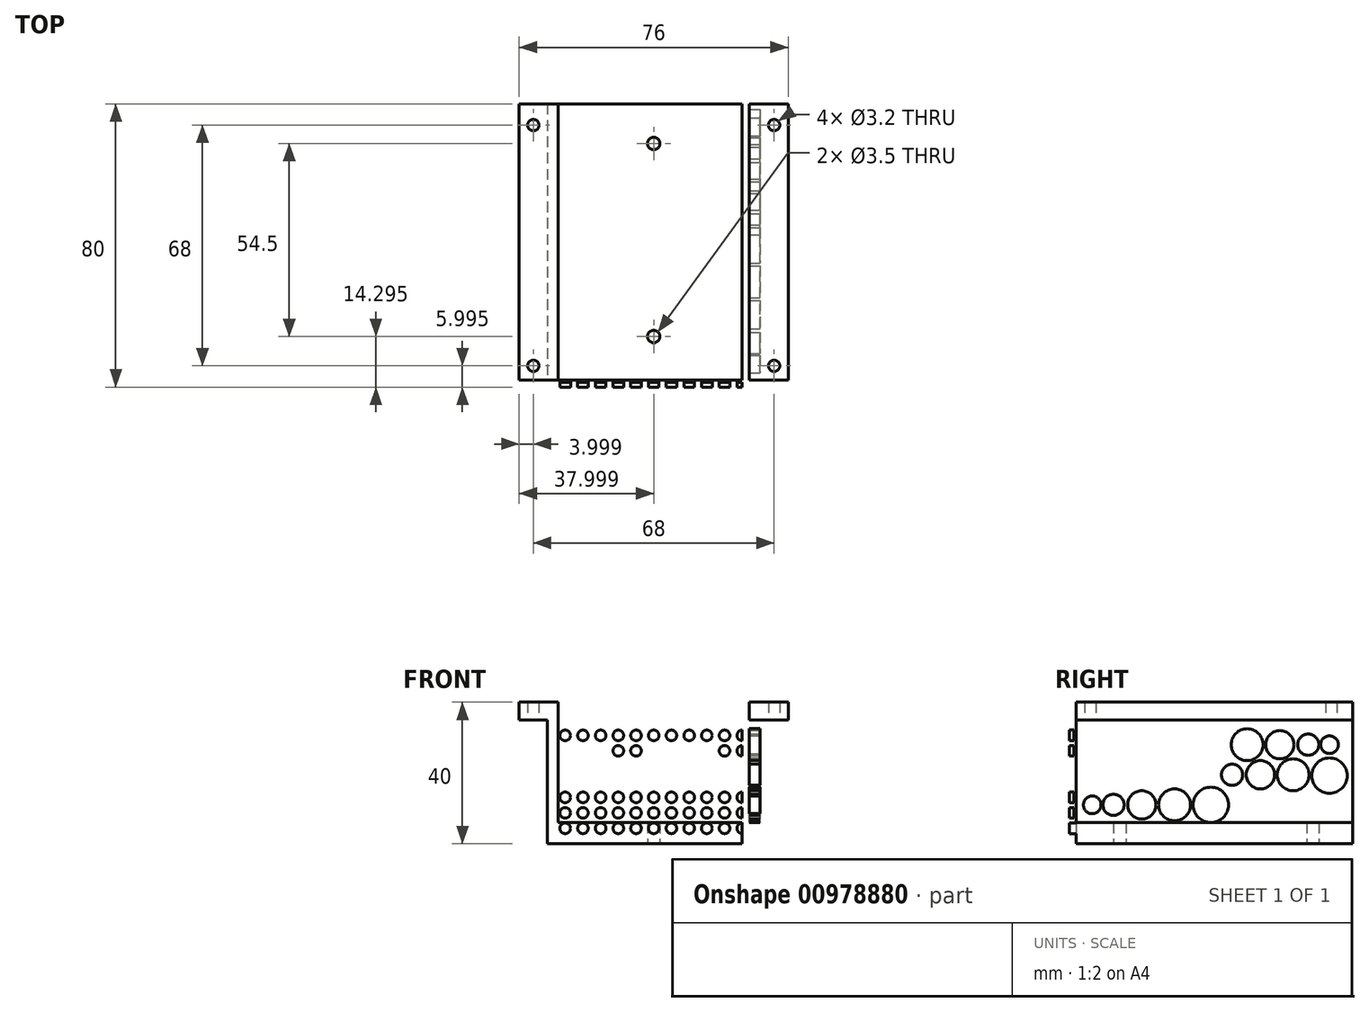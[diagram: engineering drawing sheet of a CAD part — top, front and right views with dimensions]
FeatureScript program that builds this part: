
annotation { "Feature Type Name" : "Feature", "Feature Type Description" : "" }
export const myFeature = defineFeature(function(context is Context, id is Id, definition is map)
    precondition{}
    {
        {
            var Q0;
            Q0=qCreatedBy(makeId("Top.planeOp"),FACE);
            var sketch = newSketch(context, id + "F0", { "sketchPlane" : qUnion([Q0])});
            skLineSegment(sketch, "E0.bottom", {"start": v(-26.48, 28.63) * mm, "end": v(33.52, 28.63) * mm});
            skLineSegment(sketch, "E0.top", {"start": v(-26.48, -51.37) * mm, "end": v(33.52, -51.37) * mm});
            skLineSegment(sketch, "E0.left", {"start": v(-26.48, 28.63) * mm, "end": v(-26.48, -51.37) * mm});
            skLineSegment(sketch, "E0.right", {"start": v(33.52, 28.63) * mm, "end": v(33.52, -51.37) * mm});
            skLineSegment(sketch, "E1", {"start": v(-23.48, 28.63) * mm, "end": v(-23.48, -51.37) * mm});
            skLineSegment(sketch, "E2", {"start": v(3.52, 28.63) * mm, "end": v(3.52, -51.37) * mm, "construction": true});
            skLineSegment(sketch, "E3", {"start": v(-26.48, -11.37) * mm, "end": v(33.52, -11.37) * mm, "construction": true});
            skLineSegment(sketch, "E4.MirrorCS", {"start": v(30.52, 28.63) * mm, "end": v(30.52, -51.37) * mm});
            skLineSegment(sketch, "E5", {"start": v(-23.48, -50.07) * mm, "end": v(30.52, -50.07) * mm});
            skCircle(sketch, "E6", {"center": v(3.52, -37.07) * mm, "radius": 1.75 * mm});
            skCircle(sketch, "E7", {"center": v(3.52, 17.43) * mm, "radius": 1.75 * mm});
            skLineSegment(sketch, "E8", {"start": v(-26.48, 28.63) * mm, "end": v(-34.48, 28.63) * mm});
            skLineSegment(sketch, "E9", {"start": v(-34.48, 28.63) * mm, "end": v(-34.48, -51.37) * mm});
            skLineSegment(sketch, "E10", {"start": v(-34.48, -51.37) * mm, "end": v(-26.48, -51.37) * mm});
            skLineSegment(sketch, "E11.MirrorCS", {"start": v(41.52, 28.63) * mm, "end": v(41.52, -51.37) * mm});
            skLineSegment(sketch, "E12.MirrorCS", {"start": v(33.52, 28.63) * mm, "end": v(41.52, 28.63) * mm});
            skLineSegment(sketch, "E13.MirrorCS", {"start": v(41.52, -51.37) * mm, "end": v(33.52, -51.37) * mm});
            skCircle(sketch, "E14", {"center": v(-30.48, 22.63) * mm, "radius": 1.6 * mm});
            skLineSegment(sketch, "E15", {"start": v(-34.48, -11.37) * mm, "end": v(41.52, -11.37) * mm, "construction": true});
            skCircle(sketch, "E16.MirrorC", {"center": v(-30.48, -45.37) * mm, "radius": 1.6 * mm});
            skCircle(sketch, "E17.MirrorC", {"center": v(37.52, 22.63) * mm, "radius": 1.6 * mm});
            skCircle(sketch, "E18.MirrorC", {"center": v(37.52, -45.37) * mm, "radius": 1.6 * mm});
            skSolve(sketch);
        }
        {
            var Q0;
            {var subQ0=sQuery(id+"F0.wireOp",EDGE,"E0.left");Q0=makeQuery(id+"F0.imprint","IMPRINT",FACE,{"disambiguationData":[TD([[makeQuery(id+"F0.imprint","IMPRINT",EDGE,{"derivedFrom":subQ0}),1.0]])]});}
            var Q1;
            {var subQ4=sQuery(id+"F0.wireOp",EDGE,"E0.right");Q1=makeQuery(id+"F0.imprint","IMPRINT",FACE,{"disambiguationData":[TD([[makeQuery(id+"F0.imprint","IMPRINT",EDGE,{"derivedFrom":subQ4}),-1.0]])]});}
            var Q2;
            {var subQ5=sQuery(id+"F0.wireOp",EDGE,"E5");Q2=makeQuery(id+"F0.imprint","IMPRINT",FACE,{"disambiguationData":[TD([[makeQuery(id+"F0.imprint","IMPRINT",EDGE,{"derivedFrom":subQ5}),-1.0]])]});}
            extrude(context, id + "F1", {"entities" : qUnion([Q0, Q1, Q2]), "depth" : 40 * mm, "offsetDistance" : 25 * mm});
        }
        {
            var Q0;
            {var subQ5=sQuery(id+"F0.wireOp",EDGE,"E5");Q0=makeQuery(id+"F0.imprint","IMPRINT",FACE,{"disambiguationData":[TD([[makeQuery(id+"F0.imprint","IMPRINT",EDGE,{"derivedFrom":subQ5}),1.0]])]});}
            extrude(context, id + "F2", {"entities" : qUnion([Q0]), "operationType" : NewBodyOperationType.ADD, "depth" : 6 * mm, "offsetDistance" : 25 * mm});
        }
        {
            var Q0;
            Q0=makeQuery(id+"F0.imprint","IMPRINT",FACE,{"disambiguationData":[TD([[makeQuery(id+"F0.imprint","IMPRINT",EDGE,{"derivedFrom":sQuery(id+"F0.wireOp",EDGE,"E0.left")}),-1.0]])]});
            var Q1;
            Q1=makeQuery(id+"F0.imprint","IMPRINT",FACE,{"disambiguationData":[TD([[makeQuery(id+"F0.imprint","IMPRINT",EDGE,{"derivedFrom":sQuery(id+"F0.wireOp",EDGE,"E0.right")}),1.0]])]});
            extrude(context, id + "F3", {"entities" : qUnion([Q0, Q1]), "operationType" : NewBodyOperationType.ADD, "depth" : 40 * mm, "offsetDistance" : 25 * mm, "hasSecondDirection" : true, "secondDirectionOppositeDirection" : false, "secondDirectionDepth" : 35 * mm});
        }
        {
            var Q0;
            Q0=makeQuery(id+"F1.opExtrude","SWEPT_FACE",FACE,{"disambiguationData":[OSD([sQuery(id+"F0.wireOp",EDGE,"E0.right")])]});
            var sketch = newSketch(context, id + "F4", { "sketchPlane" : qUnion([Q0])});
            skLineSegment(sketch, "E19", {"start": v(-11.37, 35) * mm, "end": v(-11.37, 0) * mm, "construction": true});
            skCircle(sketch, "E20", {"center": v(-11.37, 28) * mm, "radius": 5 * mm});
            skCircle(sketch, "E21", {"center": v(-11.37, 19.5) * mm, "radius": 2.5 * mm});
            skLineSegment(sketch, "E22", {"start": v(-44.87, 39) * mm, "end": v(-44.87, 0) * mm, "construction": true});
            skLineSegment(sketch, "E23", {"start": v(-38.26, 35) * mm, "end": v(-38.26, 0) * mm, "construction": true});
            skLineSegment(sketch, "E24", {"start": v(-25.37, 39) * mm, "end": v(-25.37, 0) * mm, "construction": true});
            skLineSegment(sketch, "E25", {"start": v(-21.54, 35) * mm, "end": v(-21.54, 0) * mm, "construction": true});
            skCircle(sketch, "E26", {"center": v(-17.37, 19.5) * mm, "radius": 3 * mm});
            skCircle(sketch, "E27", {"center": v(-25.37, 19.5) * mm, "radius": 4 * mm});
            skCircle(sketch, "E28", {"center": v(-44.87, 19.5) * mm, "radius": 5 * mm});
            skCircle(sketch, "E29", {"center": v(-34.62, 19.5) * mm, "radius": 4.5 * mm});
            skCircle(sketch, "E30.MirrorC", {"center": v(-5.37, 19.5) * mm, "radius": 3 * mm});
            skCircle(sketch, "E31.MirrorC", {"center": v(2.63, 19.5) * mm, "radius": 4 * mm});
            skCircle(sketch, "E32.MirrorC", {"center": v(11.88, 19.5) * mm, "radius": 4.5 * mm});
            skCircle(sketch, "E33.MirrorC", {"center": v(22.13, 19.25) * mm, "radius": 5 * mm});
            skCircle(sketch, "E34", {"center": v(-21.62, 28) * mm, "radius": 4.5 * mm});
            skCircle(sketch, "E35", {"center": v(-30.87, 28) * mm, "radius": 4 * mm});
            skCircle(sketch, "E36", {"center": v(-38.87, 28) * mm, "radius": 3 * mm});
            skCircle(sketch, "E37", {"center": v(-44.87, 28) * mm, "radius": 2.5 * mm});
            skCircle(sketch, "E38.MirrorC", {"center": v(-1.12, 28) * mm, "radius": 4.5 * mm});
            skCircle(sketch, "E39.MirrorC", {"center": v(8.13, 28) * mm, "radius": 4 * mm});
            skCircle(sketch, "E40.MirrorC", {"center": v(16.13, 28) * mm, "radius": 3 * mm});
            skCircle(sketch, "E41.MirrorC", {"center": v(22.13, 28) * mm, "radius": 2.5 * mm});
            skLineSegment(sketch, "E42", {"start": v(-51.37, 19.5) * mm, "end": v(28.63, 19.5) * mm, "construction": true});
            skCircle(sketch, "E43.MirrorC", {"center": v(-11.37, 11) * mm, "radius": 5 * mm});
            skCircle(sketch, "E44.MirrorC", {"center": v(-21.62, 11) * mm, "radius": 4.5 * mm});
            skCircle(sketch, "E45.MirrorC", {"center": v(-30.87, 11) * mm, "radius": 4 * mm});
            skCircle(sketch, "E46.MirrorC", {"center": v(-38.87, 11) * mm, "radius": 3 * mm});
            skCircle(sketch, "E47.MirrorC", {"center": v(-44.87, 11) * mm, "radius": 2.5 * mm});
            skCircle(sketch, "E48.MirrorC", {"center": v(-1.12, 11) * mm, "radius": 4.5 * mm});
            skCircle(sketch, "E49.MirrorC", {"center": v(8.13, 11) * mm, "radius": 4 * mm});
            skCircle(sketch, "E50.MirrorC", {"center": v(16.13, 11) * mm, "radius": 3 * mm});
            skCircle(sketch, "E51.MirrorC", {"center": v(22.13, 11) * mm, "radius": 2.5 * mm});
            skLineSegment(sketch, "E52", {"start": v(-11.37, 28) * mm, "end": v(-51.37, 28) * mm, "construction": true});
            skLineSegment(sketch, "E53", {"start": v(-51.37, 28) * mm, "end": v(28.63, 28) * mm, "construction": true});
            skSolve(sketch);
        }
        {
            var Q0;
            Q0=makeQuery(id+"F4.imprint","IMPRINT",FACE,{"disambiguationData":[TD([[makeQuery(id+"F4.imprint","IMPRINT",EDGE,{"derivedFrom":sQuery(id+"F4.wireOp",EDGE,"E37")}),1.0]])]});
            var Q1;
            Q1=makeQuery(id+"F4.imprint","IMPRINT",FACE,{"disambiguationData":[TD([[makeQuery(id+"F4.imprint","IMPRINT",EDGE,{"derivedFrom":sQuery(id+"F4.wireOp",EDGE,"E36")}),1.0]])]});
            var Q2;
            Q2=makeQuery(id+"F4.imprint","IMPRINT",FACE,{"disambiguationData":[TD([[makeQuery(id+"F4.imprint","IMPRINT",EDGE,{"derivedFrom":sQuery(id+"F4.wireOp",EDGE,"E35")}),1.0]])]});
            var Q3;
            Q3=makeQuery(id+"F4.imprint","IMPRINT",FACE,{"disambiguationData":[TD([[makeQuery(id+"F4.imprint","IMPRINT",EDGE,{"derivedFrom":sQuery(id+"F4.wireOp",EDGE,"E34")}),1.0]])]});
            var Q4;
            Q4=makeQuery(id+"F4.imprint","IMPRINT",FACE,{"disambiguationData":[TD([[makeQuery(id+"F4.imprint","IMPRINT",EDGE,{"derivedFrom":sQuery(id+"F4.wireOp",EDGE,"E20")}),1.0]])]});
            var Q5;
            Q5=makeQuery(id+"F4.imprint","IMPRINT",FACE,{"disambiguationData":[TD([[makeQuery(id+"F4.imprint","IMPRINT",EDGE,{"derivedFrom":sQuery(id+"F4.wireOp",EDGE,"E21")}),1.0]])]});
            var Q6;
            Q6=makeQuery(id+"F4.imprint","IMPRINT",FACE,{"disambiguationData":[TD([[makeQuery(id+"F4.imprint","IMPRINT",EDGE,{"derivedFrom":sQuery(id+"F4.wireOp",EDGE,"E26")}),1.0]])]});
            var Q7;
            Q7=makeQuery(id+"F4.imprint","IMPRINT",FACE,{"disambiguationData":[TD([[makeQuery(id+"F4.imprint","IMPRINT",EDGE,{"derivedFrom":sQuery(id+"F4.wireOp",EDGE,"E27")}),1.0]])]});
            var Q8;
            Q8=makeQuery(id+"F4.imprint","IMPRINT",FACE,{"disambiguationData":[TD([[makeQuery(id+"F4.imprint","IMPRINT",EDGE,{"derivedFrom":sQuery(id+"F4.wireOp",EDGE,"E29")}),1.0]])]});
            var Q9;
            Q9=makeQuery(id+"F4.imprint","IMPRINT",FACE,{"disambiguationData":[TD([[makeQuery(id+"F4.imprint","IMPRINT",EDGE,{"derivedFrom":sQuery(id+"F4.wireOp",EDGE,"E28")}),1.0]])]});
            var Q10;
            Q10=makeQuery(id+"F4.imprint","IMPRINT",FACE,{"disambiguationData":[TD([[makeQuery(id+"F4.imprint","IMPRINT",EDGE,{"derivedFrom":sQuery(id+"F4.wireOp",EDGE,"d2b82f4c-cb30-4b27-9ca2-75d97dd168ee0.MirrorC")}),-1.0]])]});
            var Q11;
            Q11=makeQuery(id+"F4.imprint","IMPRINT",FACE,{"disambiguationData":[TD([[makeQuery(id+"F4.imprint","IMPRINT",EDGE,{"derivedFrom":sQuery(id+"F4.wireOp",EDGE,"6bd1dfd8-2cc8-4437-9d2b-2d223e5973cc0.MirrorC")}),-1.0]])]});
            var Q12;
            Q12=makeQuery(id+"F4.imprint","IMPRINT",FACE,{"disambiguationData":[TD([[makeQuery(id+"F4.imprint","IMPRINT",EDGE,{"derivedFrom":sQuery(id+"F4.wireOp",EDGE,"112abbcc-eb7b-4c05-a6dc-7863f32487d60.MirrorC")}),-1.0]])]});
            var Q13;
            Q13=makeQuery(id+"F4.imprint","IMPRINT",FACE,{"disambiguationData":[TD([[makeQuery(id+"F4.imprint","IMPRINT",EDGE,{"derivedFrom":sQuery(id+"F4.wireOp",EDGE,"63fc9d48-1385-4d69-bd1f-f335cad14c7e0.MirrorC")}),-1.0]])]});
            var Q14;
            Q14=makeQuery(id+"F4.imprint","IMPRINT",FACE,{"disambiguationData":[TD([[makeQuery(id+"F4.imprint","IMPRINT",EDGE,{"derivedFrom":sQuery(id+"F4.wireOp",EDGE,"CqitQkb0-iUWd-npEw-QbOA-i5By9fwf5P85")}),1.0]])]});
            var Q15;
            Q15=makeQuery(id+"F4.imprint","IMPRINT",FACE,{"disambiguationData":[TD([[makeQuery(id+"F4.imprint","IMPRINT",EDGE,{"derivedFrom":sQuery(id+"F4.wireOp",EDGE,"b05cfdfd-f439-45fa-b4f9-9b1710cce5d10.MirrorC")}),1.0]])]});
            var Q16;
            Q16=makeQuery(id+"F4.imprint","IMPRINT",FACE,{"disambiguationData":[TD([[makeQuery(id+"F4.imprint","IMPRINT",EDGE,{"derivedFrom":sQuery(id+"F4.wireOp",EDGE,"E30.MirrorC")}),-1.0]])]});
            var Q17;
            Q17=makeQuery(id+"F4.imprint","IMPRINT",FACE,{"disambiguationData":[TD([[makeQuery(id+"F4.imprint","IMPRINT",EDGE,{"derivedFrom":sQuery(id+"F4.wireOp",EDGE,"E38.MirrorC")}),-1.0]])]});
            var Q18;
            Q18=makeQuery(id+"F4.imprint","IMPRINT",FACE,{"disambiguationData":[TD([[makeQuery(id+"F4.imprint","IMPRINT",EDGE,{"derivedFrom":sQuery(id+"F4.wireOp",EDGE,"E31.MirrorC")}),-1.0]])]});
            var Q19;
            Q19=makeQuery(id+"F4.imprint","IMPRINT",FACE,{"disambiguationData":[TD([[makeQuery(id+"F4.imprint","IMPRINT",EDGE,{"derivedFrom":sQuery(id+"F4.wireOp",EDGE,"2864415c-c3ac-41cb-945e-1ae6a54a86a40.MirrorC")}),1.0]])]});
            var Q20;
            Q20=makeQuery(id+"F4.imprint","IMPRINT",FACE,{"disambiguationData":[TD([[makeQuery(id+"F4.imprint","IMPRINT",EDGE,{"derivedFrom":sQuery(id+"F4.wireOp",EDGE,"E32.MirrorC")}),-1.0]])]});
            var Q21;
            Q21=makeQuery(id+"F4.imprint","IMPRINT",FACE,{"disambiguationData":[TD([[makeQuery(id+"F4.imprint","IMPRINT",EDGE,{"derivedFrom":sQuery(id+"F4.wireOp",EDGE,"E39.MirrorC")}),-1.0]])]});
            var Q22;
            Q22=makeQuery(id+"F4.imprint","IMPRINT",FACE,{"disambiguationData":[TD([[makeQuery(id+"F4.imprint","IMPRINT",EDGE,{"derivedFrom":sQuery(id+"F4.wireOp",EDGE,"E40.MirrorC")}),-1.0]])]});
            var Q23;
            Q23=makeQuery(id+"F4.imprint","IMPRINT",FACE,{"disambiguationData":[TD([[makeQuery(id+"F4.imprint","IMPRINT",EDGE,{"derivedFrom":sQuery(id+"F4.wireOp",EDGE,"E41.MirrorC")}),-1.0]])]});
            var Q24;
            Q24=makeQuery(id+"F4.imprint","IMPRINT",FACE,{"disambiguationData":[TD([[makeQuery(id+"F4.imprint","IMPRINT",EDGE,{"derivedFrom":sQuery(id+"F4.wireOp",EDGE,"E33.MirrorC")}),-1.0]])]});
            var Q25;
            Q25=makeQuery(id+"F4.imprint","IMPRINT",FACE,{"disambiguationData":[TD([[makeQuery(id+"F4.imprint","IMPRINT",EDGE,{"derivedFrom":sQuery(id+"F4.wireOp",EDGE,"b64800c5-5fc1-485e-8181-1b029b5031790.MirrorC")}),1.0]])]});
            var Q26;
            Q26=makeQuery(id+"F4.imprint","IMPRINT",FACE,{"disambiguationData":[TD([[makeQuery(id+"F4.imprint","IMPRINT",EDGE,{"derivedFrom":sQuery(id+"F4.wireOp",EDGE,"3597d698-ec06-4dc3-ab4d-8b58906ce14e0.MirrorC")}),1.0]])]});
            var Q27;
            Q27=makeQuery(id+"F4.imprint","IMPRINT",FACE,{"disambiguationData":[TD([[makeQuery(id+"F4.imprint","IMPRINT",EDGE,{"derivedFrom":sQuery(id+"F4.wireOp",EDGE,"E47.MirrorC")}),-1.0]])]});
            var Q28;
            Q28=makeQuery(id+"F4.imprint","IMPRINT",FACE,{"disambiguationData":[TD([[makeQuery(id+"F4.imprint","IMPRINT",EDGE,{"derivedFrom":sQuery(id+"F4.wireOp",EDGE,"E46.MirrorC")}),-1.0]])]});
            var Q29;
            Q29=makeQuery(id+"F4.imprint","IMPRINT",FACE,{"disambiguationData":[TD([[makeQuery(id+"F4.imprint","IMPRINT",EDGE,{"derivedFrom":sQuery(id+"F4.wireOp",EDGE,"E45.MirrorC")}),-1.0]])]});
            var Q30;
            Q30=makeQuery(id+"F4.imprint","IMPRINT",FACE,{"disambiguationData":[TD([[makeQuery(id+"F4.imprint","IMPRINT",EDGE,{"derivedFrom":sQuery(id+"F4.wireOp",EDGE,"E44.MirrorC")}),-1.0]])]});
            var Q31;
            Q31=makeQuery(id+"F4.imprint","IMPRINT",FACE,{"disambiguationData":[TD([[makeQuery(id+"F4.imprint","IMPRINT",EDGE,{"derivedFrom":sQuery(id+"F4.wireOp",EDGE,"E43.MirrorC")}),-1.0]])]});
            var Q32;
            Q32=makeQuery(id+"F4.imprint","IMPRINT",FACE,{"disambiguationData":[TD([[makeQuery(id+"F4.imprint","IMPRINT",EDGE,{"derivedFrom":sQuery(id+"F4.wireOp",EDGE,"E48.MirrorC")}),1.0]])]});
            var Q33;
            Q33=makeQuery(id+"F4.imprint","IMPRINT",FACE,{"disambiguationData":[TD([[makeQuery(id+"F4.imprint","IMPRINT",EDGE,{"derivedFrom":sQuery(id+"F4.wireOp",EDGE,"E49.MirrorC")}),1.0]])]});
            var Q34;
            Q34=makeQuery(id+"F4.imprint","IMPRINT",FACE,{"disambiguationData":[TD([[makeQuery(id+"F4.imprint","IMPRINT",EDGE,{"derivedFrom":sQuery(id+"F4.wireOp",EDGE,"E50.MirrorC")}),1.0]])]});
            var Q35;
            Q35=makeQuery(id+"F4.imprint","IMPRINT",FACE,{"disambiguationData":[TD([[makeQuery(id+"F4.imprint","IMPRINT",EDGE,{"derivedFrom":sQuery(id+"F4.wireOp",EDGE,"E51.MirrorC")}),1.0]])]});
            extrude(context, id + "F5", {"entities" : qUnion([Q0, Q1, Q2, Q3, Q4, Q5, Q6, Q7, Q8, Q9, Q10, Q11, Q12, Q13, Q14, Q15, Q16, Q17, Q18, Q19, Q20, Q21, Q22, Q23, Q24, Q25, Q26, Q27, Q28, Q29, Q30, Q31, Q32, Q33, Q34, Q35]), "operationType" : NewBodyOperationType.REMOVE, "oppositeDirection" : true, "depth" : 5 * mm, "offsetDistance" : 25 * mm});
        }
        {
            var Q0;
            Q0=makeQuery(id+"F3.boolean.opBoolean","MERGE",FACE,{"derivedFrom":[makeQuery(id+"F1.opExtrude","SWEPT_FACE",FACE,{"disambiguationData":[OSD([sQuery(id+"F0.wireOp",EDGE,"E0.top")])]}),makeQuery(id+"F3.opExtrude","SWEPT_FACE",FACE,{"disambiguationData":[OSD([sQuery(id+"F0.wireOp",EDGE,"E10")])]}),makeQuery(id+"F3.opExtrude","SWEPT_FACE",FACE,{"disambiguationData":[OSD([sQuery(id+"F0.wireOp",EDGE,"E13.MirrorCS")])]})]});
            var sketch = newSketch(context, id + "F6", { "sketchPlane" : qUnion([Q0])});
            skLineSegment(sketch, "E54", {"start": v(3.52, 40) * mm, "end": v(3.52, 0) * mm, "construction": true});
            skLineSegment(sketch, "E55", {"start": v(-26.48, 17.5) * mm, "end": v(33.52, 17.5) * mm, "construction": true});
            skLineSegment(sketch, "E56", {"start": v(-26.48, 35) * mm, "end": v(33.52, 35) * mm, "construction": true});
            skLineSegment(sketch, "E57", {"start": v(-26.48, 30.62) * mm, "end": v(33.52, 30.63) * mm, "construction": true});
            skLineSegment(sketch, "E58", {"start": v(33.52, 26.25) * mm, "end": v(-26.48, 26.25) * mm, "construction": true});
            skLineSegment(sketch, "E59", {"start": v(-26.48, 21.88) * mm, "end": v(33.52, 21.88) * mm, "construction": true});
            skLineSegment(sketch, "E60", {"start": v(-1.48, 35) * mm, "end": v(-1.48, 0) * mm, "construction": true});
            skLineSegment(sketch, "E61", {"start": v(-6.48, 35) * mm, "end": v(-6.48, 0) * mm, "construction": true});
            skLineSegment(sketch, "E62", {"start": v(-11.48, 35) * mm, "end": v(-11.48, 0) * mm, "construction": true});
            skLineSegment(sketch, "E63", {"start": v(-16.48, 35) * mm, "end": v(-16.48, 0) * mm, "construction": true});
            skLineSegment(sketch, "E64", {"start": v(-21.48, 35) * mm, "end": v(-21.48, 0) * mm, "construction": true});
            skLineSegment(sketch, "E65.MirrorCS", {"start": v(8.52, 35) * mm, "end": v(8.52, 0) * mm, "construction": true});
            skLineSegment(sketch, "E66.MirrorCS", {"start": v(13.52, 35) * mm, "end": v(13.52, 0) * mm, "construction": true});
            skLineSegment(sketch, "E67.MirrorCS", {"start": v(18.52, 35) * mm, "end": v(18.52, 0) * mm, "construction": true});
            skLineSegment(sketch, "E68.MirrorCS", {"start": v(23.52, 35) * mm, "end": v(23.52, 0) * mm, "construction": true});
            skLineSegment(sketch, "E69.MirrorCS", {"start": v(28.52, 35) * mm, "end": v(28.52, 0) * mm, "construction": true});
            skLineSegment(sketch, "E70.MirrorCS", {"start": v(-26.48, 13.12) * mm, "end": v(33.52, 13.12) * mm, "construction": true});
            skLineSegment(sketch, "E71.MirrorCS", {"start": v(33.52, 8.75) * mm, "end": v(-26.48, 8.75) * mm, "construction": true});
            skLineSegment(sketch, "E72.MirrorCS", {"start": v(-26.48, 4.38) * mm, "end": v(33.52, 4.37) * mm, "construction": true});
            skCircle(sketch, "E73", {"center": v(-21.48, 35) * mm, "radius": 1.5 * mm});
            skCircle(sketch, "E74", {"center": v(-16.48, 35) * mm, "radius": 1.5 * mm});
            skCircle(sketch, "E75", {"center": v(-11.48, 35) * mm, "radius": 1.5 * mm});
            skCircle(sketch, "E76", {"center": v(-6.48, 35) * mm, "radius": 1.5 * mm});
            skCircle(sketch, "E77", {"center": v(-1.48, 35) * mm, "radius": 1.5 * mm});
            skCircle(sketch, "E78", {"center": v(3.52, 35) * mm, "radius": 1.5 * mm});
            skCircle(sketch, "E79", {"center": v(8.52, 35) * mm, "radius": 1.5 * mm});
            skCircle(sketch, "E80", {"center": v(13.52, 35) * mm, "radius": 1.5 * mm});
            skCircle(sketch, "E81", {"center": v(18.52, 35) * mm, "radius": 1.5 * mm});
            skCircle(sketch, "E82", {"center": v(23.52, 35) * mm, "radius": 1.5 * mm});
            skCircle(sketch, "E83", {"center": v(28.52, 35) * mm, "radius": 1.5 * mm});
            skCircle(sketch, "E84.MirrorC", {"center": v(-21.48, 26.25) * mm, "radius": 1.5 * mm});
            skCircle(sketch, "E85.MirrorC", {"center": v(-16.48, 26.25) * mm, "radius": 1.5 * mm});
            skCircle(sketch, "E86.MirrorC", {"center": v(-11.48, 26.25) * mm, "radius": 1.5 * mm});
            skCircle(sketch, "E87.MirrorC", {"center": v(-6.48, 26.25) * mm, "radius": 1.5 * mm});
            skCircle(sketch, "E88.MirrorC", {"center": v(-1.48, 26.25) * mm, "radius": 1.5 * mm});
            skCircle(sketch, "E89.MirrorC", {"center": v(3.52, 26.25) * mm, "radius": 1.5 * mm});
            skCircle(sketch, "E90.MirrorC", {"center": v(8.52, 26.25) * mm, "radius": 1.5 * mm});
            skCircle(sketch, "E91.MirrorC", {"center": v(13.52, 26.25) * mm, "radius": 1.5 * mm});
            skCircle(sketch, "E92.MirrorC", {"center": v(18.52, 26.25) * mm, "radius": 1.5 * mm});
            skCircle(sketch, "E93.MirrorC", {"center": v(23.52, 26.25) * mm, "radius": 1.5 * mm});
            skCircle(sketch, "E94.MirrorC", {"center": v(28.52, 26.25) * mm, "radius": 1.5 * mm});
            skCircle(sketch, "E95.MirrorC", {"center": v(-21.48, 17.5) * mm, "radius": 1.5 * mm});
            skCircle(sketch, "E96.MirrorC", {"center": v(-16.48, 17.5) * mm, "radius": 1.5 * mm});
            skCircle(sketch, "E97.MirrorC", {"center": v(-11.48, 17.5) * mm, "radius": 1.5 * mm});
            skCircle(sketch, "E98.MirrorC", {"center": v(-6.48, 17.5) * mm, "radius": 1.5 * mm});
            skCircle(sketch, "E99.MirrorC", {"center": v(-1.48, 17.5) * mm, "radius": 1.5 * mm});
            skCircle(sketch, "E100.MirrorC", {"center": v(3.52, 17.5) * mm, "radius": 1.5 * mm});
            skCircle(sketch, "E101.MirrorC", {"center": v(8.52, 17.5) * mm, "radius": 1.5 * mm});
            skCircle(sketch, "E102.MirrorC", {"center": v(13.52, 17.5) * mm, "radius": 1.5 * mm});
            skCircle(sketch, "E103.MirrorC", {"center": v(18.52, 17.5) * mm, "radius": 1.5 * mm});
            skCircle(sketch, "E104.MirrorC", {"center": v(23.52, 17.5) * mm, "radius": 1.5 * mm});
            skCircle(sketch, "E105.MirrorC", {"center": v(28.52, 17.5) * mm, "radius": 1.5 * mm});
            skCircle(sketch, "E106.MirrorC", {"center": v(28.52, 8.75) * mm, "radius": 1.5 * mm});
            skCircle(sketch, "E107.MirrorC", {"center": v(23.52, 8.75) * mm, "radius": 1.5 * mm});
            skCircle(sketch, "E108.MirrorC", {"center": v(18.52, 8.75) * mm, "radius": 1.5 * mm});
            skCircle(sketch, "E109.MirrorC", {"center": v(13.52, 8.75) * mm, "radius": 1.5 * mm});
            skCircle(sketch, "E110.MirrorC", {"center": v(8.52, 8.75) * mm, "radius": 1.5 * mm});
            skCircle(sketch, "E111.MirrorC", {"center": v(3.52, 8.75) * mm, "radius": 1.5 * mm});
            skCircle(sketch, "E112.MirrorC", {"center": v(-1.48, 8.75) * mm, "radius": 1.5 * mm});
            skCircle(sketch, "E113.MirrorC", {"center": v(-6.48, 8.75) * mm, "radius": 1.5 * mm});
            skCircle(sketch, "E114.MirrorC", {"center": v(-21.48, 8.75) * mm, "radius": 1.5 * mm});
            skCircle(sketch, "E115.MirrorC", {"center": v(-16.48, 8.75) * mm, "radius": 1.5 * mm});
            skCircle(sketch, "E116.MirrorC", {"center": v(-11.48, 8.75) * mm, "radius": 1.5 * mm});
            skLineSegment(sketch, "E117", {"start": v(-26.48, 32.81) * mm, "end": v(33.52, 32.81) * mm, "construction": true});
            skCircle(sketch, "E118.MirrorC", {"center": v(8.52, 30.62) * mm, "radius": 1.5 * mm});
            skCircle(sketch, "E119.MirrorC", {"center": v(-21.48, 30.62) * mm, "radius": 1.5 * mm});
            skCircle(sketch, "E120.MirrorC", {"center": v(28.52, 30.63) * mm, "radius": 1.5 * mm});
            skCircle(sketch, "E121.MirrorC", {"center": v(-16.48, 30.62) * mm, "radius": 1.5 * mm});
            skCircle(sketch, "E122.MirrorC", {"center": v(23.52, 30.62) * mm, "radius": 1.5 * mm});
            skCircle(sketch, "E123.MirrorC", {"center": v(-6.48, 30.62) * mm, "radius": 1.5 * mm});
            skCircle(sketch, "E124.MirrorC", {"center": v(13.52, 30.62) * mm, "radius": 1.5 * mm});
            skCircle(sketch, "E125.MirrorC", {"center": v(-11.48, 30.62) * mm, "radius": 1.5 * mm});
            skCircle(sketch, "E126.MirrorC", {"center": v(18.52, 30.62) * mm, "radius": 1.5 * mm});
            skCircle(sketch, "E127.MirrorC", {"center": v(3.52, 30.62) * mm, "radius": 1.5 * mm});
            skCircle(sketch, "E128.MirrorC", {"center": v(-1.48, 30.62) * mm, "radius": 1.5 * mm});
            skCircle(sketch, "E129.MirrorC", {"center": v(8.52, 21.88) * mm, "radius": 1.5 * mm});
            skCircle(sketch, "E130.MirrorC", {"center": v(-11.48, 21.88) * mm, "radius": 1.5 * mm});
            skCircle(sketch, "E131.MirrorC", {"center": v(-6.48, 21.88) * mm, "radius": 1.5 * mm});
            skCircle(sketch, "E132.MirrorC", {"center": v(-16.48, 21.88) * mm, "radius": 1.5 * mm});
            skCircle(sketch, "E133.MirrorC", {"center": v(13.52, 21.88) * mm, "radius": 1.5 * mm});
            skCircle(sketch, "E134.MirrorC", {"center": v(28.52, 21.88) * mm, "radius": 1.5 * mm});
            skCircle(sketch, "E135.MirrorC", {"center": v(-21.48, 21.88) * mm, "radius": 1.5 * mm});
            skCircle(sketch, "E136.MirrorC", {"center": v(23.52, 21.88) * mm, "radius": 1.5 * mm});
            skCircle(sketch, "E137.MirrorC", {"center": v(18.52, 21.88) * mm, "radius": 1.5 * mm});
            skCircle(sketch, "E138.MirrorC", {"center": v(-1.48, 21.88) * mm, "radius": 1.5 * mm});
            skCircle(sketch, "E139.MirrorC", {"center": v(3.52, 21.88) * mm, "radius": 1.5 * mm});
            skCircle(sketch, "E140.MirrorC", {"center": v(3.52, 13.12) * mm, "radius": 1.5 * mm});
            skCircle(sketch, "E141.MirrorC", {"center": v(8.52, 4.38) * mm, "radius": 1.5 * mm});
            skCircle(sketch, "E142.MirrorC", {"center": v(-11.48, 4.38) * mm, "radius": 1.5 * mm});
            skCircle(sketch, "E143.MirrorC", {"center": v(-1.48, 13.12) * mm, "radius": 1.5 * mm});
            skCircle(sketch, "E144.MirrorC", {"center": v(-21.48, 4.38) * mm, "radius": 1.5 * mm});
            skCircle(sketch, "E145.MirrorC", {"center": v(18.52, 13.12) * mm, "radius": 1.5 * mm});
            skCircle(sketch, "E146.MirrorC", {"center": v(28.52, 13.12) * mm, "radius": 1.5 * mm});
            skCircle(sketch, "E147.MirrorC", {"center": v(3.52, 4.38) * mm, "radius": 1.5 * mm});
            skCircle(sketch, "E148.MirrorC", {"center": v(28.52, 4.37) * mm, "radius": 1.5 * mm});
            skCircle(sketch, "E149.MirrorC", {"center": v(-6.48, 13.12) * mm, "radius": 1.5 * mm});
            skCircle(sketch, "E150.MirrorC", {"center": v(23.52, 13.12) * mm, "radius": 1.5 * mm});
            skCircle(sketch, "E151.MirrorC", {"center": v(23.52, 4.38) * mm, "radius": 1.5 * mm});
            skCircle(sketch, "E152.MirrorC", {"center": v(-21.48, 13.12) * mm, "radius": 1.5 * mm});
            skCircle(sketch, "E153.MirrorC", {"center": v(13.52, 4.38) * mm, "radius": 1.5 * mm});
            skCircle(sketch, "E154.MirrorC", {"center": v(13.52, 13.12) * mm, "radius": 1.5 * mm});
            skCircle(sketch, "E155.MirrorC", {"center": v(-16.48, 4.38) * mm, "radius": 1.5 * mm});
            skCircle(sketch, "E156.MirrorC", {"center": v(18.52, 4.38) * mm, "radius": 1.5 * mm});
            skCircle(sketch, "E157.MirrorC", {"center": v(-16.48, 13.12) * mm, "radius": 1.5 * mm});
            skCircle(sketch, "E158.MirrorC", {"center": v(-6.48, 4.38) * mm, "radius": 1.5 * mm});
            skCircle(sketch, "E159.MirrorC", {"center": v(8.52, 13.12) * mm, "radius": 1.5 * mm});
            skCircle(sketch, "E160.MirrorC", {"center": v(-1.48, 4.38) * mm, "radius": 1.5 * mm});
            skCircle(sketch, "E161.MirrorC", {"center": v(-11.48, 13.12) * mm, "radius": 1.5 * mm});
            skSolve(sketch);
        }
        {
            var Q0;
            Q0=makeQuery(id+"F6.imprint","IMPRINT",FACE,{"disambiguationData":[TD([[makeQuery(id+"F6.imprint","IMPRINT",EDGE,{"derivedFrom":sQuery(id+"F6.wireOp",EDGE,"E79")}),1.0]])]});
            var Q1;
            Q1=makeQuery(id+"F6.imprint","IMPRINT",FACE,{"disambiguationData":[TD([[makeQuery(id+"F6.imprint","IMPRINT",EDGE,{"derivedFrom":sQuery(id+"F6.wireOp",EDGE,"E80")}),1.0]])]});
            var Q2;
            Q2=makeQuery(id+"F6.imprint","IMPRINT",FACE,{"disambiguationData":[TD([[makeQuery(id+"F6.imprint","IMPRINT",EDGE,{"derivedFrom":sQuery(id+"F6.wireOp",EDGE,"E124.MirrorC")}),-1.0]])]});
            var Q3;
            Q3=makeQuery(id+"F6.imprint","IMPRINT",FACE,{"disambiguationData":[TD([[makeQuery(id+"F6.imprint","IMPRINT",EDGE,{"derivedFrom":sQuery(id+"F6.wireOp",EDGE,"E118.MirrorC")}),-1.0]])]});
            var Q4;
            Q4=makeQuery(id+"F6.imprint","IMPRINT",FACE,{"disambiguationData":[TD([[makeQuery(id+"F6.imprint","IMPRINT",EDGE,{"derivedFrom":sQuery(id+"F6.wireOp",EDGE,"E127.MirrorC")}),-1.0]])]});
            var Q5;
            Q5=makeQuery(id+"F6.imprint","IMPRINT",FACE,{"disambiguationData":[TD([[makeQuery(id+"F6.imprint","IMPRINT",EDGE,{"derivedFrom":sQuery(id+"F6.wireOp",EDGE,"E78")}),1.0]])]});
            var Q6;
            Q6=makeQuery(id+"F6.imprint","IMPRINT",FACE,{"disambiguationData":[TD([[makeQuery(id+"F6.imprint","IMPRINT",EDGE,{"derivedFrom":sQuery(id+"F6.wireOp",EDGE,"E77")}),1.0]])]});
            var Q7;
            Q7=makeQuery(id+"F6.imprint","IMPRINT",FACE,{"disambiguationData":[TD([[makeQuery(id+"F6.imprint","IMPRINT",EDGE,{"derivedFrom":sQuery(id+"F6.wireOp",EDGE,"E128.MirrorC")}),-1.0]])]});
            var Q8;
            Q8=makeQuery(id+"F6.imprint","IMPRINT",FACE,{"disambiguationData":[TD([[makeQuery(id+"F6.imprint","IMPRINT",EDGE,{"derivedFrom":sQuery(id+"F6.wireOp",EDGE,"E123.MirrorC")}),-1.0]])]});
            var Q9;
            Q9=makeQuery(id+"F6.imprint","IMPRINT",FACE,{"disambiguationData":[TD([[makeQuery(id+"F6.imprint","IMPRINT",EDGE,{"derivedFrom":sQuery(id+"F6.wireOp",EDGE,"E125.MirrorC")}),-1.0]])]});
            var Q10;
            Q10=makeQuery(id+"F6.imprint","IMPRINT",FACE,{"disambiguationData":[TD([[makeQuery(id+"F6.imprint","IMPRINT",EDGE,{"derivedFrom":sQuery(id+"F6.wireOp",EDGE,"E75")}),1.0]])]});
            var Q11;
            Q11=makeQuery(id+"F6.imprint","IMPRINT",FACE,{"disambiguationData":[TD([[makeQuery(id+"F6.imprint","IMPRINT",EDGE,{"derivedFrom":sQuery(id+"F6.wireOp",EDGE,"E76")}),1.0]])]});
            var Q12;
            Q12=makeQuery(id+"F6.imprint","IMPRINT",FACE,{"disambiguationData":[TD([[makeQuery(id+"F6.imprint","IMPRINT",EDGE,{"derivedFrom":sQuery(id+"F6.wireOp",EDGE,"E74")}),1.0]])]});
            var Q13;
            Q13=makeQuery(id+"F6.imprint","IMPRINT",FACE,{"disambiguationData":[TD([[makeQuery(id+"F6.imprint","IMPRINT",EDGE,{"derivedFrom":sQuery(id+"F6.wireOp",EDGE,"E73")}),1.0]])]});
            var Q14;
            Q14=makeQuery(id+"F6.imprint","IMPRINT",FACE,{"disambiguationData":[TD([[makeQuery(id+"F6.imprint","IMPRINT",EDGE,{"derivedFrom":sQuery(id+"F6.wireOp",EDGE,"E119.MirrorC")}),-1.0]])]});
            var Q15;
            Q15=makeQuery(id+"F6.imprint","IMPRINT",FACE,{"disambiguationData":[TD([[makeQuery(id+"F6.imprint","IMPRINT",EDGE,{"derivedFrom":sQuery(id+"F6.wireOp",EDGE,"E121.MirrorC")}),-1.0]])]});
            var Q16;
            Q16=makeQuery(id+"F6.imprint","IMPRINT",FACE,{"disambiguationData":[TD([[makeQuery(id+"F6.imprint","IMPRINT",EDGE,{"derivedFrom":sQuery(id+"F6.wireOp",EDGE,"E85.MirrorC")}),1.0]])]});
            var Q17;
            Q17=makeQuery(id+"F6.imprint","IMPRINT",FACE,{"disambiguationData":[TD([[makeQuery(id+"F6.imprint","IMPRINT",EDGE,{"derivedFrom":sQuery(id+"F6.wireOp",EDGE,"E84.MirrorC")}),1.0]])]});
            var Q18;
            Q18=makeQuery(id+"F6.imprint","IMPRINT",FACE,{"disambiguationData":[TD([[makeQuery(id+"F6.imprint","IMPRINT",EDGE,{"derivedFrom":sQuery(id+"F6.wireOp",EDGE,"E86.MirrorC")}),1.0]])]});
            var Q19;
            Q19=makeQuery(id+"F6.imprint","IMPRINT",FACE,{"disambiguationData":[TD([[makeQuery(id+"F6.imprint","IMPRINT",EDGE,{"derivedFrom":sQuery(id+"F6.wireOp",EDGE,"E87.MirrorC")}),1.0]])]});
            var Q20;
            Q20=makeQuery(id+"F6.imprint","IMPRINT",FACE,{"disambiguationData":[TD([[makeQuery(id+"F6.imprint","IMPRINT",EDGE,{"derivedFrom":sQuery(id+"F6.wireOp",EDGE,"E88.MirrorC")}),1.0]])]});
            var Q21;
            Q21=makeQuery(id+"F6.imprint","IMPRINT",FACE,{"disambiguationData":[TD([[makeQuery(id+"F6.imprint","IMPRINT",EDGE,{"derivedFrom":sQuery(id+"F6.wireOp",EDGE,"E89.MirrorC")}),1.0]])]});
            var Q22;
            Q22=makeQuery(id+"F6.imprint","IMPRINT",FACE,{"disambiguationData":[TD([[makeQuery(id+"F6.imprint","IMPRINT",EDGE,{"derivedFrom":sQuery(id+"F6.wireOp",EDGE,"E90.MirrorC")}),1.0]])]});
            var Q23;
            Q23=makeQuery(id+"F6.imprint","IMPRINT",FACE,{"disambiguationData":[TD([[makeQuery(id+"F6.imprint","IMPRINT",EDGE,{"derivedFrom":sQuery(id+"F6.wireOp",EDGE,"E91.MirrorC")}),1.0]])]});
            var Q24;
            Q24=makeQuery(id+"F6.imprint","IMPRINT",FACE,{"disambiguationData":[TD([[makeQuery(id+"F6.imprint","IMPRINT",EDGE,{"derivedFrom":sQuery(id+"F6.wireOp",EDGE,"E92.MirrorC")}),1.0]])]});
            var Q25;
            Q25=makeQuery(id+"F6.imprint","IMPRINT",FACE,{"disambiguationData":[TD([[makeQuery(id+"F6.imprint","IMPRINT",EDGE,{"derivedFrom":sQuery(id+"F6.wireOp",EDGE,"E126.MirrorC")}),-1.0]])]});
            var Q26;
            Q26=makeQuery(id+"F6.imprint","IMPRINT",FACE,{"disambiguationData":[TD([[makeQuery(id+"F6.imprint","IMPRINT",EDGE,{"derivedFrom":sQuery(id+"F6.wireOp",EDGE,"E81")}),1.0]])]});
            var Q27;
            Q27=makeQuery(id+"F6.imprint","IMPRINT",FACE,{"disambiguationData":[TD([[makeQuery(id+"F6.imprint","IMPRINT",EDGE,{"derivedFrom":sQuery(id+"F6.wireOp",EDGE,"E82")}),1.0]])]});
            var Q28;
            Q28=makeQuery(id+"F6.imprint","IMPRINT",FACE,{"disambiguationData":[TD([[makeQuery(id+"F6.imprint","IMPRINT",EDGE,{"derivedFrom":sQuery(id+"F6.wireOp",EDGE,"E83")}),1.0]])]});
            var Q29;
            Q29=makeQuery(id+"F6.imprint","IMPRINT",FACE,{"disambiguationData":[TD([[makeQuery(id+"F6.imprint","IMPRINT",EDGE,{"derivedFrom":sQuery(id+"F6.wireOp",EDGE,"E120.MirrorC")}),-1.0]])]});
            var Q30;
            Q30=makeQuery(id+"F6.imprint","IMPRINT",FACE,{"disambiguationData":[TD([[makeQuery(id+"F6.imprint","IMPRINT",EDGE,{"derivedFrom":sQuery(id+"F6.wireOp",EDGE,"E122.MirrorC")}),-1.0]])]});
            var Q31;
            Q31=makeQuery(id+"F6.imprint","IMPRINT",FACE,{"disambiguationData":[TD([[makeQuery(id+"F6.imprint","IMPRINT",EDGE,{"derivedFrom":sQuery(id+"F6.wireOp",EDGE,"E93.MirrorC")}),-1.0]])]});
            var Q32;
            Q32=makeQuery(id+"F6.imprint","IMPRINT",FACE,{"disambiguationData":[TD([[makeQuery(id+"F6.imprint","IMPRINT",EDGE,{"derivedFrom":sQuery(id+"F6.wireOp",EDGE,"E94.MirrorC")}),-1.0]])]});
            var Q33;
            Q33=makeQuery(id+"F6.imprint","IMPRINT",FACE,{"disambiguationData":[TD([[makeQuery(id+"F6.imprint","IMPRINT",EDGE,{"derivedFrom":sQuery(id+"F6.wireOp",EDGE,"E134.MirrorC")}),1.0]])]});
            var Q34;
            Q34=makeQuery(id+"F6.imprint","IMPRINT",FACE,{"disambiguationData":[TD([[makeQuery(id+"F6.imprint","IMPRINT",EDGE,{"derivedFrom":sQuery(id+"F6.wireOp",EDGE,"E136.MirrorC")}),1.0]])]});
            var Q35;
            Q35=makeQuery(id+"F6.imprint","IMPRINT",FACE,{"disambiguationData":[TD([[makeQuery(id+"F6.imprint","IMPRINT",EDGE,{"derivedFrom":sQuery(id+"F6.wireOp",EDGE,"E137.MirrorC")}),1.0]])]});
            var Q36;
            Q36=makeQuery(id+"F6.imprint","IMPRINT",FACE,{"disambiguationData":[TD([[makeQuery(id+"F6.imprint","IMPRINT",EDGE,{"derivedFrom":sQuery(id+"F6.wireOp",EDGE,"E133.MirrorC")}),1.0]])]});
            var Q37;
            Q37=makeQuery(id+"F6.imprint","IMPRINT",FACE,{"disambiguationData":[TD([[makeQuery(id+"F6.imprint","IMPRINT",EDGE,{"derivedFrom":sQuery(id+"F6.wireOp",EDGE,"E129.MirrorC")}),1.0]])]});
            var Q38;
            Q38=makeQuery(id+"F6.imprint","IMPRINT",FACE,{"disambiguationData":[TD([[makeQuery(id+"F6.imprint","IMPRINT",EDGE,{"derivedFrom":sQuery(id+"F6.wireOp",EDGE,"E139.MirrorC")}),1.0]])]});
            var Q39;
            Q39=makeQuery(id+"F6.imprint","IMPRINT",FACE,{"disambiguationData":[TD([[makeQuery(id+"F6.imprint","IMPRINT",EDGE,{"derivedFrom":sQuery(id+"F6.wireOp",EDGE,"E138.MirrorC")}),1.0]])]});
            var Q40;
            Q40=makeQuery(id+"F6.imprint","IMPRINT",FACE,{"disambiguationData":[TD([[makeQuery(id+"F6.imprint","IMPRINT",EDGE,{"derivedFrom":sQuery(id+"F6.wireOp",EDGE,"E131.MirrorC")}),1.0]])]});
            var Q41;
            Q41=makeQuery(id+"F6.imprint","IMPRINT",FACE,{"disambiguationData":[TD([[makeQuery(id+"F6.imprint","IMPRINT",EDGE,{"derivedFrom":sQuery(id+"F6.wireOp",EDGE,"E98.MirrorC")}),1.0]])]});
            var Q42;
            Q42=makeQuery(id+"F6.imprint","IMPRINT",FACE,{"disambiguationData":[TD([[makeQuery(id+"F6.imprint","IMPRINT",EDGE,{"derivedFrom":sQuery(id+"F6.wireOp",EDGE,"E99.MirrorC")}),1.0]])]});
            var Q43;
            Q43=makeQuery(id+"F6.imprint","IMPRINT",FACE,{"disambiguationData":[TD([[makeQuery(id+"F6.imprint","IMPRINT",EDGE,{"derivedFrom":sQuery(id+"F6.wireOp",EDGE,"E100.MirrorC")}),1.0]])]});
            var Q44;
            Q44=makeQuery(id+"F6.imprint","IMPRINT",FACE,{"disambiguationData":[TD([[makeQuery(id+"F6.imprint","IMPRINT",EDGE,{"derivedFrom":sQuery(id+"F6.wireOp",EDGE,"E101.MirrorC")}),1.0]])]});
            var Q45;
            Q45=makeQuery(id+"F6.imprint","IMPRINT",FACE,{"disambiguationData":[TD([[makeQuery(id+"F6.imprint","IMPRINT",EDGE,{"derivedFrom":sQuery(id+"F6.wireOp",EDGE,"E102.MirrorC")}),1.0]])]});
            var Q46;
            Q46=makeQuery(id+"F6.imprint","IMPRINT",FACE,{"disambiguationData":[TD([[makeQuery(id+"F6.imprint","IMPRINT",EDGE,{"derivedFrom":sQuery(id+"F6.wireOp",EDGE,"E103.MirrorC")}),1.0]])]});
            var Q47;
            Q47=makeQuery(id+"F6.imprint","IMPRINT",FACE,{"disambiguationData":[TD([[makeQuery(id+"F6.imprint","IMPRINT",EDGE,{"derivedFrom":sQuery(id+"F6.wireOp",EDGE,"E104.MirrorC")}),1.0]])]});
            var Q48;
            Q48=makeQuery(id+"F6.imprint","IMPRINT",FACE,{"disambiguationData":[TD([[makeQuery(id+"F6.imprint","IMPRINT",EDGE,{"derivedFrom":sQuery(id+"F6.wireOp",EDGE,"E105.MirrorC")}),1.0]])]});
            var Q49;
            Q49=makeQuery(id+"F6.imprint","IMPRINT",FACE,{"disambiguationData":[TD([[makeQuery(id+"F6.imprint","IMPRINT",EDGE,{"derivedFrom":sQuery(id+"F6.wireOp",EDGE,"E130.MirrorC")}),1.0]])]});
            var Q50;
            Q50=makeQuery(id+"F6.imprint","IMPRINT",FACE,{"disambiguationData":[TD([[makeQuery(id+"F6.imprint","IMPRINT",EDGE,{"derivedFrom":sQuery(id+"F6.wireOp",EDGE,"E132.MirrorC")}),1.0]])]});
            var Q51;
            Q51=makeQuery(id+"F6.imprint","IMPRINT",FACE,{"disambiguationData":[TD([[makeQuery(id+"F6.imprint","IMPRINT",EDGE,{"derivedFrom":sQuery(id+"F6.wireOp",EDGE,"E135.MirrorC")}),1.0]])]});
            var Q52;
            Q52=makeQuery(id+"F6.imprint","IMPRINT",FACE,{"disambiguationData":[TD([[makeQuery(id+"F6.imprint","IMPRINT",EDGE,{"derivedFrom":sQuery(id+"F6.wireOp",EDGE,"E95.MirrorC")}),1.0]])]});
            var Q53;
            Q53=makeQuery(id+"F6.imprint","IMPRINT",FACE,{"disambiguationData":[TD([[makeQuery(id+"F6.imprint","IMPRINT",EDGE,{"derivedFrom":sQuery(id+"F6.wireOp",EDGE,"E96.MirrorC")}),1.0]])]});
            var Q54;
            Q54=makeQuery(id+"F6.imprint","IMPRINT",FACE,{"disambiguationData":[TD([[makeQuery(id+"F6.imprint","IMPRINT",EDGE,{"derivedFrom":sQuery(id+"F6.wireOp",EDGE,"E97.MirrorC")}),1.0]])]});
            var Q55;
            Q55=makeQuery(id+"F6.imprint","IMPRINT",FACE,{"disambiguationData":[TD([[makeQuery(id+"F6.imprint","IMPRINT",EDGE,{"derivedFrom":sQuery(id+"F6.wireOp",EDGE,"E161.MirrorC")}),-1.0]])]});
            var Q56;
            Q56=makeQuery(id+"F6.imprint","IMPRINT",FACE,{"disambiguationData":[TD([[makeQuery(id+"F6.imprint","IMPRINT",EDGE,{"derivedFrom":sQuery(id+"F6.wireOp",EDGE,"E157.MirrorC")}),-1.0]])]});
            var Q57;
            Q57=makeQuery(id+"F6.imprint","IMPRINT",FACE,{"disambiguationData":[TD([[makeQuery(id+"F6.imprint","IMPRINT",EDGE,{"derivedFrom":sQuery(id+"F6.wireOp",EDGE,"E152.MirrorC")}),-1.0]])]});
            var Q58;
            Q58=makeQuery(id+"F6.imprint","IMPRINT",FACE,{"disambiguationData":[TD([[makeQuery(id+"F6.imprint","IMPRINT",EDGE,{"derivedFrom":sQuery(id+"F6.wireOp",EDGE,"E114.MirrorC")}),1.0]])]});
            var Q59;
            Q59=makeQuery(id+"F6.imprint","IMPRINT",FACE,{"disambiguationData":[TD([[makeQuery(id+"F6.imprint","IMPRINT",EDGE,{"derivedFrom":sQuery(id+"F6.wireOp",EDGE,"E115.MirrorC")}),-1.0]])]});
            var Q60;
            Q60=makeQuery(id+"F6.imprint","IMPRINT",FACE,{"disambiguationData":[TD([[makeQuery(id+"F6.imprint","IMPRINT",EDGE,{"derivedFrom":sQuery(id+"F6.wireOp",EDGE,"E116.MirrorC")}),1.0]])]});
            var Q61;
            Q61=makeQuery(id+"F6.imprint","IMPRINT",FACE,{"disambiguationData":[TD([[makeQuery(id+"F6.imprint","IMPRINT",EDGE,{"derivedFrom":sQuery(id+"F6.wireOp",EDGE,"E113.MirrorC")}),-1.0]])]});
            var Q62;
            Q62=makeQuery(id+"F6.imprint","IMPRINT",FACE,{"disambiguationData":[TD([[makeQuery(id+"F6.imprint","IMPRINT",EDGE,{"derivedFrom":sQuery(id+"F6.wireOp",EDGE,"E112.MirrorC")}),1.0]])]});
            var Q63;
            Q63=makeQuery(id+"F6.imprint","IMPRINT",FACE,{"disambiguationData":[TD([[makeQuery(id+"F6.imprint","IMPRINT",EDGE,{"derivedFrom":sQuery(id+"F6.wireOp",EDGE,"E111.MirrorC")}),-1.0]])]});
            var Q64;
            Q64=makeQuery(id+"F6.imprint","IMPRINT",FACE,{"disambiguationData":[TD([[makeQuery(id+"F6.imprint","IMPRINT",EDGE,{"derivedFrom":sQuery(id+"F6.wireOp",EDGE,"E110.MirrorC")}),-1.0]])]});
            var Q65;
            Q65=makeQuery(id+"F6.imprint","IMPRINT",FACE,{"disambiguationData":[TD([[makeQuery(id+"F6.imprint","IMPRINT",EDGE,{"derivedFrom":sQuery(id+"F6.wireOp",EDGE,"E109.MirrorC")}),1.0]])]});
            var Q66;
            Q66=makeQuery(id+"F6.imprint","IMPRINT",FACE,{"disambiguationData":[TD([[makeQuery(id+"F6.imprint","IMPRINT",EDGE,{"derivedFrom":sQuery(id+"F6.wireOp",EDGE,"E154.MirrorC")}),-1.0]])]});
            var Q67;
            Q67=makeQuery(id+"F6.imprint","IMPRINT",FACE,{"disambiguationData":[TD([[makeQuery(id+"F6.imprint","IMPRINT",EDGE,{"derivedFrom":sQuery(id+"F6.wireOp",EDGE,"E159.MirrorC")}),-1.0]])]});
            var Q68;
            Q68=makeQuery(id+"F6.imprint","IMPRINT",FACE,{"disambiguationData":[TD([[makeQuery(id+"F6.imprint","IMPRINT",EDGE,{"derivedFrom":sQuery(id+"F6.wireOp",EDGE,"E140.MirrorC")}),-1.0]])]});
            var Q69;
            Q69=makeQuery(id+"F6.imprint","IMPRINT",FACE,{"disambiguationData":[TD([[makeQuery(id+"F6.imprint","IMPRINT",EDGE,{"derivedFrom":sQuery(id+"F6.wireOp",EDGE,"E143.MirrorC")}),-1.0]])]});
            var Q70;
            Q70=makeQuery(id+"F6.imprint","IMPRINT",FACE,{"disambiguationData":[TD([[makeQuery(id+"F6.imprint","IMPRINT",EDGE,{"derivedFrom":sQuery(id+"F6.wireOp",EDGE,"E149.MirrorC")}),-1.0]])]});
            var Q71;
            Q71=makeQuery(id+"F6.imprint","IMPRINT",FACE,{"disambiguationData":[TD([[makeQuery(id+"F6.imprint","IMPRINT",EDGE,{"derivedFrom":sQuery(id+"F6.wireOp",EDGE,"E108.MirrorC")}),1.0]])]});
            var Q72;
            Q72=makeQuery(id+"F6.imprint","IMPRINT",FACE,{"disambiguationData":[TD([[makeQuery(id+"F6.imprint","IMPRINT",EDGE,{"derivedFrom":sQuery(id+"F6.wireOp",EDGE,"E145.MirrorC")}),-1.0]])]});
            var Q73;
            Q73=makeQuery(id+"F6.imprint","IMPRINT",FACE,{"disambiguationData":[TD([[makeQuery(id+"F6.imprint","IMPRINT",EDGE,{"derivedFrom":sQuery(id+"F6.wireOp",EDGE,"E106.MirrorC")}),1.0]])]});
            var Q74;
            Q74=makeQuery(id+"F6.imprint","IMPRINT",FACE,{"disambiguationData":[TD([[makeQuery(id+"F6.imprint","IMPRINT",EDGE,{"derivedFrom":sQuery(id+"F6.wireOp",EDGE,"E146.MirrorC")}),-1.0]])]});
            var Q75;
            Q75=makeQuery(id+"F6.imprint","IMPRINT",FACE,{"disambiguationData":[TD([[makeQuery(id+"F6.imprint","IMPRINT",EDGE,{"derivedFrom":sQuery(id+"F6.wireOp",EDGE,"E150.MirrorC")}),-1.0]])]});
            var Q76;
            Q76=makeQuery(id+"F6.imprint","IMPRINT",FACE,{"disambiguationData":[TD([[makeQuery(id+"F6.imprint","IMPRINT",EDGE,{"derivedFrom":sQuery(id+"F6.wireOp",EDGE,"E107.MirrorC")}),1.0]])]});
            extrude(context, id + "F7", {"entities" : qUnion([Q0, Q1, Q2, Q3, Q4, Q5, Q6, Q7, Q8, Q9, Q10, Q11, Q12, Q13, Q14, Q15, Q16, Q17, Q18, Q19, Q20, Q21, Q22, Q23, Q24, Q25, Q26, Q27, Q28, Q29, Q30, Q31, Q32, Q33, Q34, Q35, Q36, Q37, Q38, Q39, Q40, Q41, Q42, Q43, Q44, Q45, Q46, Q47, Q48, Q49, Q50, Q51, Q52, Q53, Q54, Q55, Q56, Q57, Q58, Q59, Q60, Q61, Q62, Q63, Q64, Q65, Q66, Q67, Q68, Q69, Q70, Q71, Q72, Q73, Q74, Q75, Q76]), "operationType" : NewBodyOperationType.REMOVE, "oppositeDirection" : true, "depth" : 2 * mm, "offsetDistance" : 25 * mm});
        }
    });
